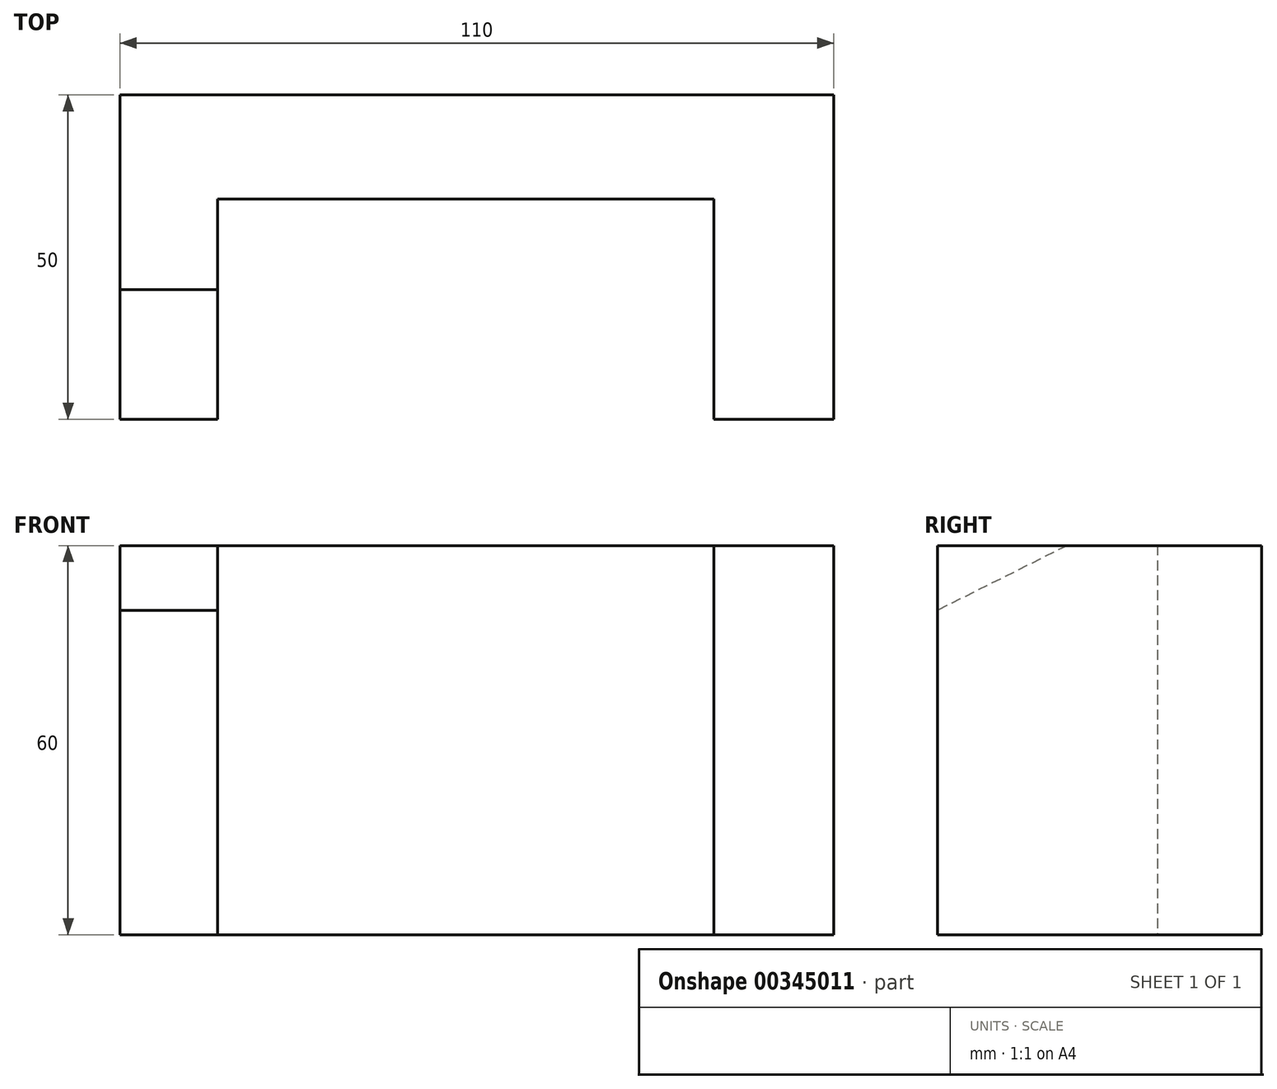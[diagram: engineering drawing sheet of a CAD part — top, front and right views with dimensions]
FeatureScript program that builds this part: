
annotation { "Feature Type Name" : "Feature", "Feature Type Description" : "" }
export const myFeature = defineFeature(function(context is Context, id is Id, definition is map)
    precondition{}
    {
        {
            var Q0;
            Q0=qCreatedBy(makeId("Top.planeOp"),FACE);
            var sketch = newSketch(context, id + "F0", { "sketchPlane" : qUnion([Q0])});
            skLineSegment(sketch, "E0", {"start": v(-54.7, -18.5) * mm, "end": v(-54.7, 31.5) * mm});
            skLineSegment(sketch, "E1", {"start": v(-54.7, 31.5) * mm, "end": v(55.3, 31.5) * mm});
            skLineSegment(sketch, "E2", {"start": v(55.3, 31.5) * mm, "end": v(55.3, -18.5) * mm});
            skLineSegment(sketch, "E3", {"start": v(55.3, -18.5) * mm, "end": v(36.83, -18.5) * mm});
            skLineSegment(sketch, "E4", {"start": v(-54.7, -18.5) * mm, "end": v(-39.7, -18.5) * mm});
            skLineSegment(sketch, "E5", {"start": v(-39.7, -18.5) * mm, "end": v(-39.7, 15.43) * mm});
            skLineSegment(sketch, "E6", {"start": v(-39.7, 15.43) * mm, "end": v(36.83, 15.43) * mm});
            skLineSegment(sketch, "E7", {"start": v(36.83, 15.43) * mm, "end": v(36.83, -18.5) * mm});
            skSolve(sketch);
        }
        {
            var Q0;
            Q0 = qSketchRegion(id + "F0", true);
            extrude(context, id + "F1", {"entities" : qUnion([Q0]), "depth" : 60 * mm});
        }
        {
            var Q0;
            Q0=makeQuery(id+"F1.opExtrude","SWEPT_FACE",FACE,{"disambiguationData":[OSD([sQuery(id+"F0.wireOp",EDGE,"E0")])]});
            var sketch = newSketch(context, id + "F2", { "sketchPlane" : qUnion([Q0])});
            skLineSegment(sketch, "E8", {"start": v(-1.5, 60) * mm, "end": v(18.5, 50) * mm});
            skSolve(sketch);
        }
        {
            var Q0;
            {var subQ0=sQuery(id+"F2.wireOp",EDGE,"E8");Q0=makeQuery(id+"F2.imprint","IMPRINT",FACE,{"disambiguationData":[TD([[makeQuery(id+"F2.imprint","IMPRINT",EDGE,{"derivedFrom":subQ0}),1.0]])]});}
            extrude(context, id + "F3", {"entities" : qUnion([Q0]), "operationType" : NewBodyOperationType.REMOVE, "oppositeDirection" : true, "depth" : 25 * mm});
        }
    });
